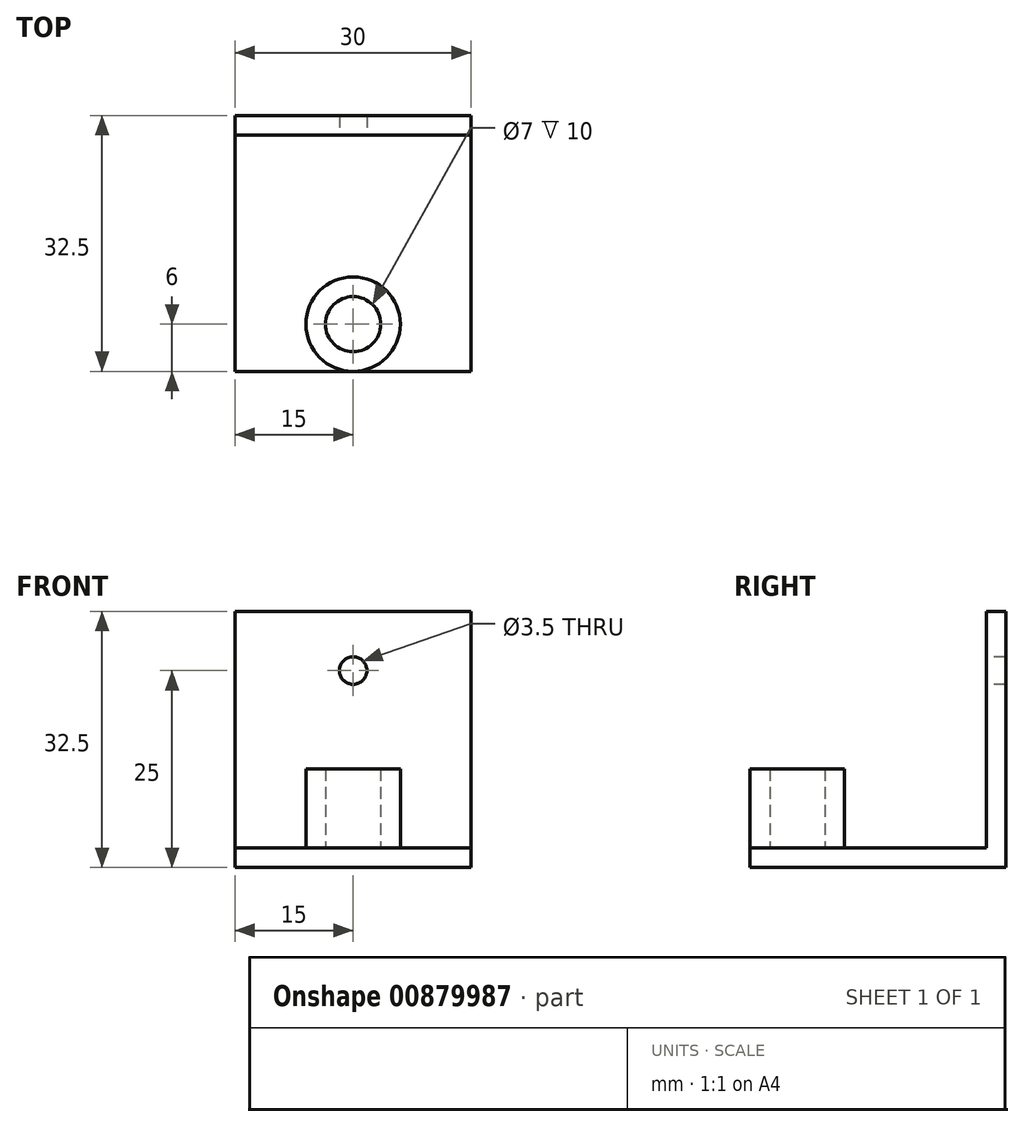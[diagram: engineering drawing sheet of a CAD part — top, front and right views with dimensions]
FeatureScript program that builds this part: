
annotation { "Feature Type Name" : "Feature", "Feature Type Description" : "" }
export const myFeature = defineFeature(function(context is Context, id is Id, definition is map)
    precondition{}
    {
        {
            var Q0;
            Q0=qCreatedBy(makeId("Top.planeOp"),FACE);
            var sketch = newSketch(context, id + "F0", { "sketchPlane" : qUnion([Q0])});
            skLineSegment(sketch, "E0.bottom", {"start": v(-15, -16.25) * mm, "end": v(15, -16.25) * mm});
            skLineSegment(sketch, "E0.top", {"start": v(-15, 16.25) * mm, "end": v(15, 16.25) * mm});
            skLineSegment(sketch, "E0.left", {"start": v(-15, -16.25) * mm, "end": v(-15, 16.25) * mm});
            skLineSegment(sketch, "E0.right", {"start": v(15, -16.25) * mm, "end": v(15, 16.25) * mm});
            skPoint(sketch, "E0.middle", {"position": v(0, 0) * mm});
            skLineSegment(sketch, "E1", {"start": v(-15, 13.75) * mm, "end": v(15, 13.75) * mm});
            skCircle(sketch, "E2", {"center": v(0, -10.25) * mm, "radius": 3.5 * mm});
            skCircle(sketch, "E3", {"center": v(0, -10.25) * mm, "radius": 6 * mm});
            skSolve(sketch);
        }
        {
            var Q0;
            {var subQ3=sQuery(id+"F0.wireOp",EDGE,"E1");Q0=makeQuery(id+"F0.imprint","IMPRINT",FACE,{"disambiguationData":[TD([[makeQuery(id+"F0.imprint","IMPRINT",EDGE,{"derivedFrom":subQ3}),-1.0]])]});}
            var Q1;
            Q1=makeQuery(id+"F0.imprint","IMPRINT",FACE,{"disambiguationData":[TD([[makeQuery(id+"F0.imprint","IMPRINT",EDGE,{"derivedFrom":sQuery(id+"F0.wireOp",EDGE,"E2")}),1.0]])]});
            var Q2;
            Q2=makeQuery(id+"F0.imprint","IMPRINT",FACE,{"disambiguationData":[TD([[makeQuery(id+"F0.imprint","IMPRINT",EDGE,{"derivedFrom":sQuery(id+"F0.wireOp",EDGE,"E2")}),-1.0]])]});
            var Q3;
            {var subQ0=sQuery(id+"F0.wireOp",EDGE,"E0.top");Q3=makeQuery(id+"F0.imprint","IMPRINT",FACE,{"disambiguationData":[TD([[makeQuery(id+"F0.imprint","IMPRINT",EDGE,{"derivedFrom":subQ0}),-1.0]])]});}
            extrude(context, id + "F1", {"entities" : qUnion([Q0, Q1, Q2, Q3]), "depth" : 2.5 * mm, "offsetDistance" : 25 * mm});
        }
        {
            var Q0;
            Q0=makeQuery(id+"F0.imprint","IMPRINT",FACE,{"disambiguationData":[TD([[makeQuery(id+"F0.imprint","IMPRINT",EDGE,{"derivedFrom":sQuery(id+"F0.wireOp",EDGE,"E2")}),-1.0]])]});
            extrude(context, id + "F2", {"entities" : qUnion([Q0]), "operationType" : NewBodyOperationType.ADD, "depth" : (10 + 2.5) * mm, "offsetDistance" : 25 * mm});
        }
        {
            var Q0;
            {var subQ0=sQuery(id+"F0.wireOp",EDGE,"E0.top");Q0=makeQuery(id+"F0.imprint","IMPRINT",FACE,{"disambiguationData":[TD([[makeQuery(id+"F0.imprint","IMPRINT",EDGE,{"derivedFrom":subQ0}),-1.0]])]});}
            extrude(context, id + "F3", {"entities" : qUnion([Q0]), "operationType" : NewBodyOperationType.ADD, "depth" : (30 + 2.5) * mm, "offsetDistance" : 25 * mm});
        }
        {
            var Q0;
            Q0=makeQuery(id+"F3.opExtrude","SWEPT_FACE",FACE,{"disambiguationData":[OSD([sQuery(id+"F0.wireOp",EDGE,"E1")])]});
            var sketch = newSketch(context, id + "F4", { "sketchPlane" : qUnion([Q0])});
            skLineSegment(sketch, "E4", {"start": v(-15, 17.5) * mm, "end": v(15, 17.5) * mm, "construction": true});
            skLineSegment(sketch, "E5", {"start": v(0, 17.5) * mm, "end": v(0, 32.5) * mm, "construction": true});
            skPoint(sketch, "E6", {"position": v(0, 25) * mm});
            skCircle(sketch, "E7", {"center": v(0, 25) * mm, "radius": 1.75 * mm});
            skSolve(sketch);
        }
        {
            var Q0;
            Q0=makeQuery(id+"F4.imprint","IMPRINT",FACE,{"disambiguationData":[TD([[makeQuery(id+"F4.imprint","IMPRINT",EDGE,{"derivedFrom":sQuery(id+"F4.wireOp",EDGE,"E7")}),1.0]])]});
            extrude(context, id + "F5", {"entities" : qUnion([Q0]), "operationType" : NewBodyOperationType.REMOVE, "endBound" : BoundingType.THROUGH_ALL, "oppositeDirection" : true, "depth" : 25 * mm, "offsetDistance" : 25 * mm});
        }
    });
